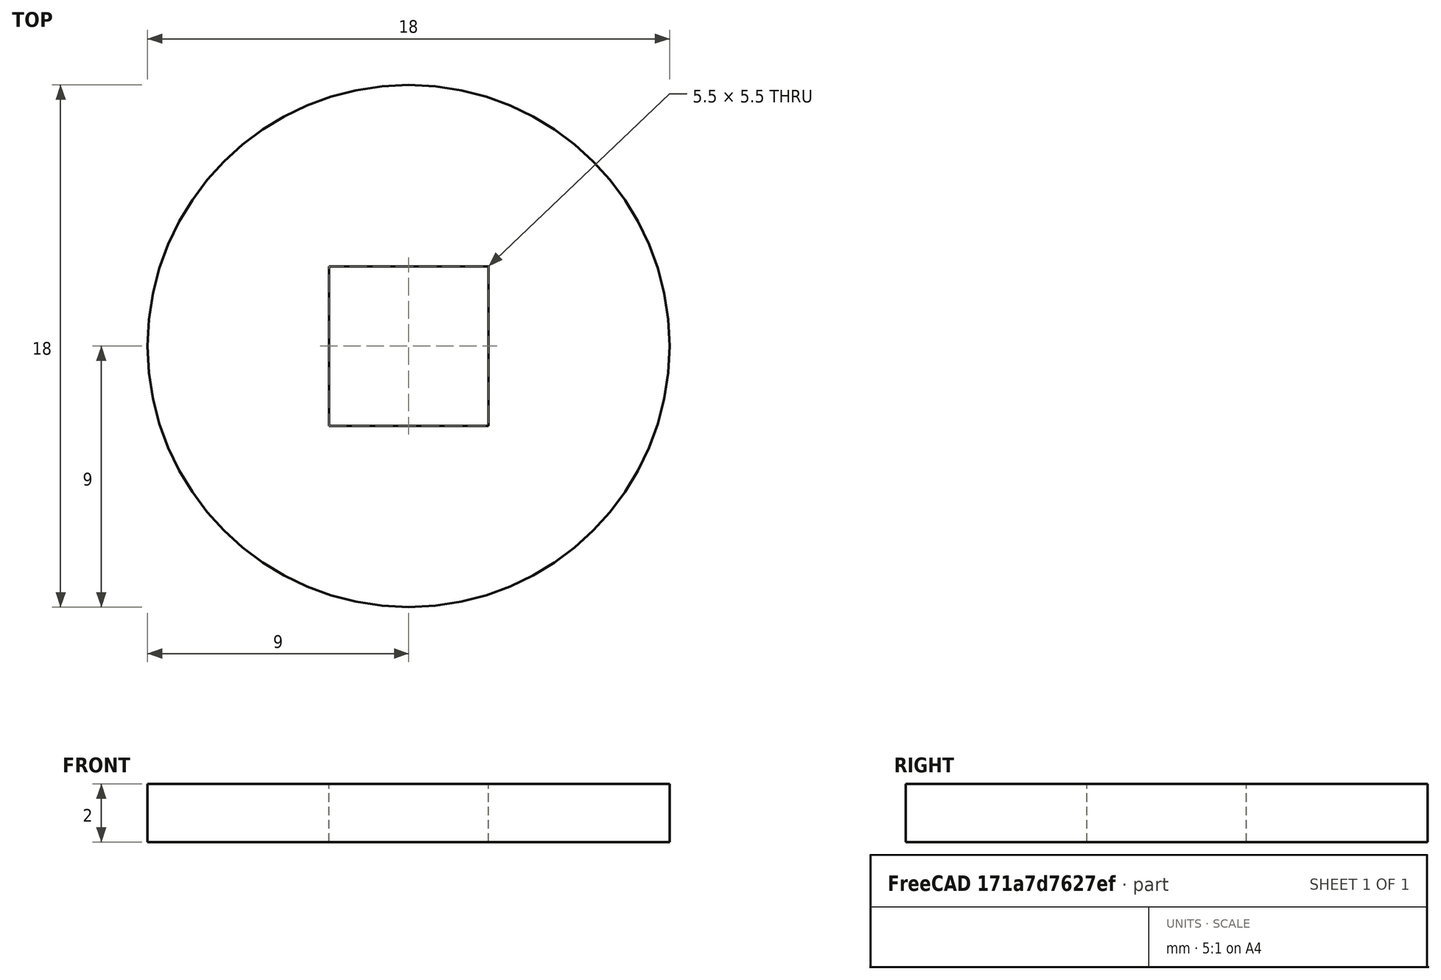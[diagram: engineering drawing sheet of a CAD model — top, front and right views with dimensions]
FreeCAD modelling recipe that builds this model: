
FCSTD DOCUMENT  (FreeCAD 0.15R4671 (Git))
Label: DIN440_CLASS_V_M5
License: CreativeCommons Attribution-ShareAlike
LicenseURL: http://creativecommons.org/licenses/by-sa/4.0/
objects: Sketcher::SketchObject×1, PartDesign::Pad×1
note: 3 computed .brp shape members not serialized (recipe doc carries the construction recipe); baked Part::Feature solids carry a one-line shape summary decoded from their .brp

FEATURE [Sketcher::SketchObject] Sketch
  sketch-geometry (5):
    g0: Circle CenterX=0 CenterY=0 CenterZ=0 NormalX=0 NormalY=0 NormalZ=1 Radius=9
    g1: LineSegment StartX=-2.75 StartY=2.75 StartZ=0 EndX=2.75 EndY=2.75 EndZ=0
    g2: LineSegment StartX=2.75 StartY=2.75 StartZ=0 EndX=2.75 EndY=-2.75 EndZ=0
    g3: LineSegment StartX=2.75 StartY=-2.75 StartZ=0 EndX=-2.75 EndY=-2.75 EndZ=0
    g4: LineSegment StartX=-2.75 StartY=-2.75 StartZ=0 EndX=-2.75 EndY=2.75 EndZ=0
  constraints (15):
    c: Coincident(g0,g-1)
    c: Radius(g0) = 9
    c: Coincident(g1,g2)
    c: Coincident(g2,g3)
    c: Coincident(g3,g4)
    c: Coincident(g4,g1)
    c: Horizontal(g1)
    c: Horizontal(g3)
    c: Vertical(g2)
    c: Vertical(g4)
    c: Equal(g1,g4)
    c: Equal(g4,g3)
    c: Equal(g3,g2)
    c: DistanceX(g1,g1) = 5.5
    c: Symmetric(g2,g1,g-1)
FEATURE [PartDesign::Pad] Pad
  Length = 2
  Length2 = 100
  Sketch = -> Sketch
  Type = 0
